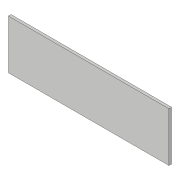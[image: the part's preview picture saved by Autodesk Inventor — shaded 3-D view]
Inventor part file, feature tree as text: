
AUTODESK INVENTOR PART (.ipt)
format: ipt  version: 2018.3 (Build 223284000, 284)  size: 71,680 bytes
history: native  units: in
note: dims shown in document units (in); Inventor stores cm internally (conversion verified against a paired STEP export)
features: extrude x1, sketch x1
ambient origin geometry x8: Origin, YZ Plane, XZ Plane, XY Plane, X Axis, Y Axis, Z Axis, Center Point
bodies: Solid1 (feature_tree)
feature tree (2):
  extrude  "Extrusion1"  Depth=0.56in
  sketch  "Sketch1"  dims[d0=1.83in d1=0.56in d2=0.03in d3=0.0in]
